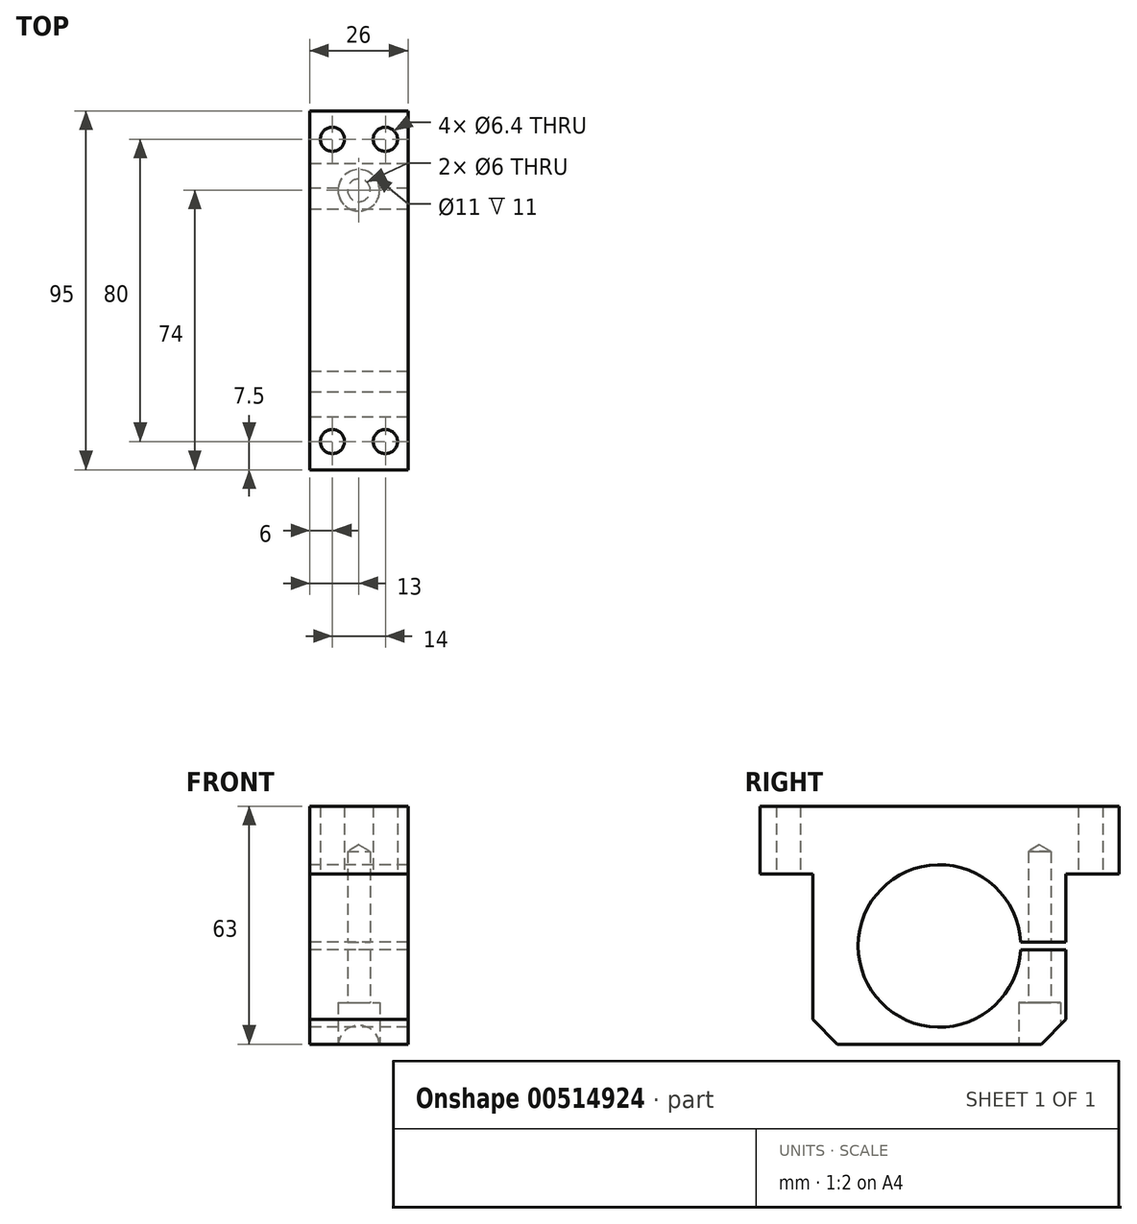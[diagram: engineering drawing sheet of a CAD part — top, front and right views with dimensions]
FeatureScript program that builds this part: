
annotation { "Feature Type Name" : "Feature", "Feature Type Description" : "" }
export const myFeature = defineFeature(function(context is Context, id is Id, definition is map)
    precondition{}
    {
        {
            var Q0;
            Q0=qCreatedBy(makeId("Right.planeOp"),FACE);
            var sketch = newSketch(context, id + "F0", { "sketchPlane" : qUnion([Q0])});
            skLineSegment(sketch, "E0.bottom", {"start": v(-27, 0) * mm, "end": v(27, 0) * mm});
            skLineSegment(sketch, "E0.left", {"start": v(-33.5, 6.5) * mm, "end": v(-33.5, 45) * mm});
            skLineSegment(sketch, "E0.right", {"start": v(33.5, 6.5) * mm, "end": v(33.5, 25) * mm});
            skLineSegment(sketch, "E1.top", {"start": v(-47.5, 63) * mm, "end": v(47.5, 63) * mm});
            skLineSegment(sketch, "E1.left", {"start": v(-47.5, 45) * mm, "end": v(-47.5, 63) * mm});
            skLineSegment(sketch, "E1.right", {"start": v(47.5, 45) * mm, "end": v(47.5, 63) * mm});
            skArc(sketch, "E2", {"start": v(21.48, 27) * mm, "mid": v(-21.5, 26) * mm, "end": v(21.48, 25) * mm});
            skLineSegment(sketch, "E3", {"start": v(33.5, 27) * mm, "end": v(21.48, 27) * mm});
            skLineSegment(sketch, "E4", {"start": v(21.48, 25) * mm, "end": v(33.5, 25) * mm});
            skLineSegment(sketch, "E5", {"start": v(-62.25, 26) * mm, "end": v(101.45, 26) * mm, "construction": true});
            skLineSegment(sketch, "E6", {"start": v(33.5, 45) * mm, "end": v(47.5, 45) * mm});
            skLineSegment(sketch, "E7", {"start": v(-33.5, 45) * mm, "end": v(-47.5, 45) * mm});
            skLineSegment(sketch, "E8", {"start": v(-33.5, 6.5) * mm, "end": v(-27, 0) * mm});
            skLineSegment(sketch, "E9", {"start": v(27, 0) * mm, "end": v(33.5, 6.5) * mm});
            skLineSegment(sketch, "E10.trimOffspring", {"start": v(33.5, 27) * mm, "end": v(33.5, 45) * mm});
            skSolve(sketch);
        }
        {
            var Q0;
            Q0=makeQuery(id+"F0.imprint","IMPRINT",FACE,{"disambiguationData":[TD([[makeQuery(id+"F0.imprint","IMPRINT",EDGE,{"derivedFrom":sQuery(id+"F0.wireOp",EDGE,"E0.bottom")}),1.0]])]});
            extrude(context, id + "F1", {"entities" : qUnion([Q0]), "depth" : 26 * mm, "offsetDistance" : 25 * mm});
        }
        {
            var Q0;
            Q0=makeQuery(id+"F1.opExtrude","SWEPT_FACE",FACE,{"disambiguationData":[OSD([sQuery(id+"F0.wireOp",EDGE,"E7")])]});
            var sketch = newSketch(context, id + "F2", { "sketchPlane" : qUnion([Q0])});
            skLineSegment(sketch, "E11.0.0", {"start": v(0, 47.5) * mm, "end": v(0, 33.5) * mm, "construction": true});
            skLineSegment(sketch, "E11.0.1", {"start": v(0, 33.5) * mm, "end": v(26, 33.5) * mm, "construction": true});
            skLineSegment(sketch, "E11.0.2", {"start": v(26, 33.5) * mm, "end": v(26, 47.5) * mm, "construction": true});
            skLineSegment(sketch, "E11.0.3", {"start": v(26, 47.5) * mm, "end": v(0, 47.5) * mm, "construction": true});
            skCircle(sketch, "E12", {"center": v(20, 40) * mm, "radius": 3.2 * mm});
            skCircle(sketch, "E13", {"center": v(6, 40) * mm, "radius": 3.2 * mm});
            skCircle(sketch, "E14.MirrorC", {"center": v(20, -40) * mm, "radius": 3.2 * mm});
            skCircle(sketch, "E15.MirrorC", {"center": v(6, -40) * mm, "radius": 3.2 * mm});
            skSolve(sketch);
        }
        {
            var Q0;
            Q0=sQuery(id+"F2.wireOp",VERTEX,"E13.center");
            var Q1;
            Q1=sQuery(id+"F2.wireOp",VERTEX,"E12.center");
            var Q2;
            Q2=sQuery(id+"F2.wireOp",VERTEX,"E14.MirrorC.center");
            var Q3;
            Q3=sQuery(id+"F2.wireOp",VERTEX,"E15.MirrorC.center");
            var Q4;
            Q4=makeQuery(id+"F1.opExtrude","SWEPT_BODY",BODY,{"disambiguationData":[OSD([sQuery(id+"F0.wireOp",EDGE,"E0.bottom"),sQuery(id+"F0.wireOp",EDGE,"E0.left"),sQuery(id+"F0.wireOp",EDGE,"E0.right"),sQuery(id+"F0.wireOp",EDGE,"E1.top"),sQuery(id+"F0.wireOp",EDGE,"E1.left"),sQuery(id+"F0.wireOp",EDGE,"E1.right"),sQuery(id+"F0.wireOp",EDGE,"E2"),sQuery(id+"F0.wireOp",EDGE,"E3"),sQuery(id+"F0.wireOp",EDGE,"E4"),sQuery(id+"F0.wireOp",EDGE,"E6"),sQuery(id+"F0.wireOp",EDGE,"E7"),sQuery(id+"F0.wireOp",EDGE,"E8"),sQuery(id+"F0.wireOp",EDGE,"E9"),sQuery(id+"F0.wireOp",EDGE,"E10.trimOffspring")])]});
            hole(context, id + "F3", {"style" : HoleStyle.SIMPLE, "endStyle" : HoleEndStyle.THROUGH, "holeDiameter" : 6.4 * mm, "majorDiameter" : 5 * mm, "isTappedThrough" : true, "tappedDepth" : 12 * mm, "tapClearance" : 3, "locations" : qUnion([Q0, Q1, Q2, Q3]), "scope" : qUnion([Q4])});
        }
        {
            var Q0;
            Q0=makeQuery(id+"F1.opExtrude","SWEPT_FACE",FACE,{"disambiguationData":[OSD([sQuery(id+"F0.wireOp",EDGE,"E0.bottom")])]});
            var sketch = newSketch(context, id + "F4", { "sketchPlane" : qUnion([Q0])});
            skCircle(sketch, "E16", {"center": v(13, -26.5) * mm, "radius": 5.5 * mm});
            skSolve(sketch);
        }
        {
            var Q0;
            Q0=sQuery(id+"F4.wireOp",VERTEX,"E16.center");
            var Q1;
            Q1=makeQuery(id+"F1.opExtrude","SWEPT_BODY",BODY,{"disambiguationData":[OSD([sQuery(id+"F0.wireOp",EDGE,"E0.bottom"),sQuery(id+"F0.wireOp",EDGE,"E0.left"),sQuery(id+"F0.wireOp",EDGE,"E0.right"),sQuery(id+"F0.wireOp",EDGE,"E1.top"),sQuery(id+"F0.wireOp",EDGE,"E1.left"),sQuery(id+"F0.wireOp",EDGE,"E1.right"),sQuery(id+"F0.wireOp",EDGE,"E2"),sQuery(id+"F0.wireOp",EDGE,"E3"),sQuery(id+"F0.wireOp",EDGE,"E4"),sQuery(id+"F0.wireOp",EDGE,"E6"),sQuery(id+"F0.wireOp",EDGE,"E7"),sQuery(id+"F0.wireOp",EDGE,"E8"),sQuery(id+"F0.wireOp",EDGE,"E9"),sQuery(id+"F0.wireOp",EDGE,"E10.trimOffspring")])]});
            hole(context, id + "F5", {"style" : HoleStyle.C_BORE, "endStyle" : HoleEndStyle.BLIND, "holeDiameter" : 6 * mm, "cBoreDiameter" : 11 * mm, "cBoreDepth" : 6 * mm, "majorDiameter" : 5 * mm, "holeDepth" : 46 * mm, "isTappedThrough" : true, "tappedDepth" : 12 * mm, "tapClearance" : 3, "locations" : qUnion([Q0]), "scope" : qUnion([Q1])});
        }
    });
